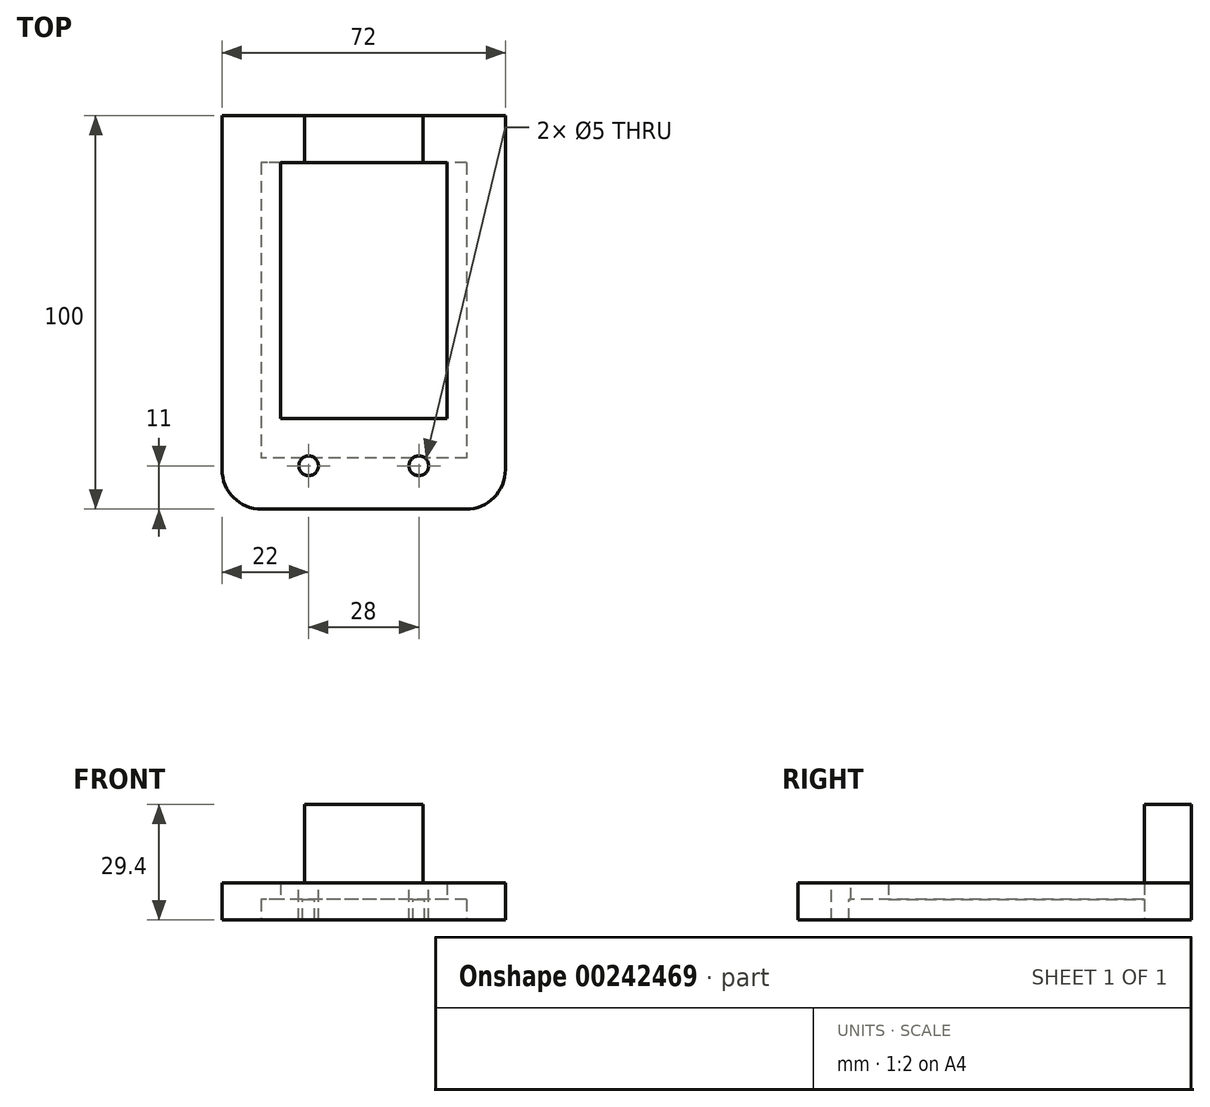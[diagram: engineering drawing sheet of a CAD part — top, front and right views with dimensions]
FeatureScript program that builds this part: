
annotation { "Feature Type Name" : "Feature", "Feature Type Description" : "" }
export const myFeature = defineFeature(function(context is Context, id is Id, definition is map)
    precondition{}
    {
        {
            var Q0;
            Q0=qCreatedBy(makeId("Top.planeOp"),FACE);
            var sketch = newSketch(context, id + "F0", { "sketchPlane" : qUnion([Q0])});
            skLineSegment(sketch, "E0.bottom", {"start": v(36, 50) * mm, "end": v(-36, 50) * mm});
            skLineSegment(sketch, "E0.top", {"start": v(36, -50) * mm, "end": v(-36, -50) * mm});
            skLineSegment(sketch, "E0.left", {"start": v(36, 50) * mm, "end": v(36, -50) * mm});
            skLineSegment(sketch, "E0.right", {"start": v(-36, 50) * mm, "end": v(-36, -50) * mm});
            skPoint(sketch, "E0.middle", {"position": v(0, 0) * mm});
            skSolve(sketch);
        }
        {
            var Q0;
            Q0=makeQuery(id+"F0.imprint","IMPRINT",FACE,{"disambiguationData":[TD([[makeQuery(id+"F0.imprint","IMPRINT",EDGE,{"derivedFrom":sQuery(id+"F0.wireOp",EDGE,"E0.bottom")}),1.0]])]});
            extrude(context, id + "F1", {"entities" : qUnion([Q0]), "depth" : 9.4 * mm});
        }
        {
            var Q0;
            Q0=makeQuery(id+"F1.opExtrude","CAP_FACE",FACE,{"disambiguationData":[OSD([sQuery(id+"F0.wireOp",EDGE,"E0.bottom"),sQuery(id+"F0.wireOp",EDGE,"E0.top"),sQuery(id+"F0.wireOp",EDGE,"E0.left"),sQuery(id+"F0.wireOp",EDGE,"E0.right")])],"isStart":true});
            var sketch = newSketch(context, id + "F2", { "sketchPlane" : qUnion([Q0])});
            skLineSegment(sketch, "E1.bottom", {"start": v(26.15, -38) * mm, "end": v(-26.15, -38) * mm});
            skLineSegment(sketch, "E1.top", {"start": v(26.15, 37) * mm, "end": v(-26.15, 37) * mm});
            skLineSegment(sketch, "E1.left", {"start": v(26.15, -38) * mm, "end": v(26.15, 37) * mm});
            skLineSegment(sketch, "E1.right", {"start": v(-26.15, -38) * mm, "end": v(-26.15, 37) * mm});
            skPoint(sketch, "E1.middle", {"position": v(0, -0.5) * mm});
            skLineSegment(sketch, "E2.bottom", {"start": v(21.1, 27) * mm, "end": v(-21.1, 27) * mm});
            skLineSegment(sketch, "E2.top", {"start": v(21.1, -38) * mm, "end": v(-21.1, -38) * mm});
            skLineSegment(sketch, "E2.left", {"start": v(21.1, 27) * mm, "end": v(21.1, -38) * mm});
            skLineSegment(sketch, "E2.right", {"start": v(-21.1, 27) * mm, "end": v(-21.1, -38) * mm});
            skPoint(sketch, "E2.middle", {"position": v(0, -5.5) * mm});
            skPoint(sketch, "E3", {"position": v(0, -38) * mm});
            skSolve(sketch);
        }
        {
            var Q0;
            Q0=makeQuery(id+"F2.imprint","IMPRINT",FACE,{"disambiguationData":[TD([[makeQuery(id+"F2.imprint","IMPRINT",EDGE,{"derivedFrom":sQuery(id+"F2.wireOp",EDGE,"E1.bottom")}),-1.0]])]});
            var Q1;
            Q1=makeQuery(id+"F2.imprint","IMPRINT",FACE,{"disambiguationData":[TD([[makeQuery(id+"F2.imprint","IMPRINT",EDGE,{"derivedFrom":sQuery(id+"F2.wireOp",EDGE,"E2.bottom")}),1.0]])]});
            var Q2;
            {var subQ5=sQuery(id+"F2.wireOp",EDGE,"E2.top");Q2=makeQuery(id+"F2.imprint","IMPRINT",FACE,{"disambiguationData":[TD([[makeQuery(id+"F2.imprint","IMPRINT",EDGE,{"derivedFrom":subQ5}),-1.0]])]});}
            extrude(context, id + "F3", {"entities" : qUnion([Q0, Q1, Q2]), "operationType" : NewBodyOperationType.REMOVE, "oppositeDirection" : true, "depth" : 5.2 * mm});
        }
        {
            var Q0;
            Q0=makeQuery(id+"F2.imprint","IMPRINT",FACE,{"disambiguationData":[TD([[makeQuery(id+"F2.imprint","IMPRINT",EDGE,{"derivedFrom":sQuery(id+"F2.wireOp",EDGE,"E2.bottom")}),1.0]])]});
            var Q1;
            {var subQ5=sQuery(id+"F2.wireOp",EDGE,"E2.top");Q1=makeQuery(id+"F2.imprint","IMPRINT",FACE,{"disambiguationData":[TD([[makeQuery(id+"F2.imprint","IMPRINT",EDGE,{"derivedFrom":subQ5}),-1.0]])]});}
            var Q2;
            Q2=makeQuery(id+"F1.opExtrude","CAP_FACE",FACE,{"disambiguationData":[OSD([sQuery(id+"F0.wireOp",EDGE,"E0.bottom"),sQuery(id+"F0.wireOp",EDGE,"E0.top"),sQuery(id+"F0.wireOp",EDGE,"E0.left"),sQuery(id+"F0.wireOp",EDGE,"E0.right")])],"isStart":false});
            extrude(context, id + "F4", {"entities" : qUnion([Q0, Q1]), "operationType" : NewBodyOperationType.REMOVE, "endBound" : BoundingType.UP_TO_SURFACE, "oppositeDirection" : true, "endBoundEntityFace" : qUnion([Q2]), "depth" : 25 * mm});
        }
        {
            var Q0;
            Q0=makeQuery(id+"F1.opExtrude","CAP_FACE",FACE,{"disambiguationData":[OSD([sQuery(id+"F0.wireOp",EDGE,"E0.bottom"),sQuery(id+"F0.wireOp",EDGE,"E0.top"),sQuery(id+"F0.wireOp",EDGE,"E0.left"),sQuery(id+"F0.wireOp",EDGE,"E0.right")])],"isStart":false});
            var sketch = newSketch(context, id + "F5", { "sketchPlane" : qUnion([Q0])});
            skLineSegment(sketch, "E4.bottom", {"start": v(-15, 50) * mm, "end": v(15, 50) * mm});
            skLineSegment(sketch, "E4.top", {"start": v(-15, 38) * mm, "end": v(15, 38) * mm});
            skLineSegment(sketch, "E4.left", {"start": v(-15, 50) * mm, "end": v(-15, 38) * mm});
            skLineSegment(sketch, "E4.right", {"start": v(15, 50) * mm, "end": v(15, 38) * mm});
            skPoint(sketch, "E5", {"position": v(0, 50) * mm});
            skSolve(sketch);
        }
        {
            var Q0;
            Q0=makeQuery(id+"F5.imprint","IMPRINT",FACE,{"disambiguationData":[TD([[makeQuery(id+"F5.imprint","IMPRINT",EDGE,{"derivedFrom":sQuery(id+"F5.wireOp",EDGE,"xHcaIH9m-dqr2-VmLf-LCX5-amg7zSHhJgyx.bottom")}),-1.0]])]});
            var Q1;
            Q1=makeQuery(id+"F5.imprint","IMPRINT",FACE,{"disambiguationData":[TD([[makeQuery(id+"F5.imprint","IMPRINT",EDGE,{"derivedFrom":sQuery(id+"F5.wireOp",EDGE,"E4.bottom")}),1.0]])]});
            extrude(context, id + "F6", {"entities" : qUnion([Q0, Q1]), "operationType" : NewBodyOperationType.ADD, "depth" : 20 * mm});
        }
        {
            var Q0;
            Q0=makeQuery(id+"F1.opExtrude","CAP_FACE",FACE,{"disambiguationData":[OSD([sQuery(id+"F0.wireOp",EDGE,"E0.bottom"),sQuery(id+"F0.wireOp",EDGE,"E0.top"),sQuery(id+"F0.wireOp",EDGE,"E0.left"),sQuery(id+"F0.wireOp",EDGE,"E0.right")])],"isStart":false});
            var sketch = newSketch(context, id + "F7", { "sketchPlane" : qUnion([Q0])});
            skLineSegment(sketch, "E6", {"start": v(-36, -39) * mm, "end": v(36, -39) * mm, "construction": true});
            skCircle(sketch, "E7", {"center": v(-14, -39) * mm, "radius": 2.5 * mm});
            skCircle(sketch, "E8", {"center": v(14, -39) * mm, "radius": 2.5 * mm});
            skSolve(sketch);
        }
        {
            var Q0;
            Q0=makeQuery(id+"F7.imprint","IMPRINT",FACE,{"disambiguationData":[TD([[makeQuery(id+"F7.imprint","IMPRINT",EDGE,{"derivedFrom":sQuery(id+"F7.wireOp",EDGE,"E7")}),1.0]])]});
            var Q1;
            Q1=makeQuery(id+"F7.imprint","IMPRINT",FACE,{"disambiguationData":[TD([[makeQuery(id+"F7.imprint","IMPRINT",EDGE,{"derivedFrom":sQuery(id+"F7.wireOp",EDGE,"E8")}),1.0]])]});
            var Q2;
            Q2=makeQuery(id+"F1.opExtrude","CAP_FACE",FACE,{"disambiguationData":[OSD([sQuery(id+"F0.wireOp",EDGE,"E0.bottom"),sQuery(id+"F0.wireOp",EDGE,"E0.top"),sQuery(id+"F0.wireOp",EDGE,"E0.left"),sQuery(id+"F0.wireOp",EDGE,"E0.right")])],"isStart":true});
            extrude(context, id + "F8", {"entities" : qUnion([Q0, Q1]), "operationType" : NewBodyOperationType.REMOVE, "endBound" : BoundingType.UP_TO_SURFACE, "oppositeDirection" : true, "endBoundEntityFace" : qUnion([Q2]), "depth" : 25 * mm});
        }
        {
            var Q0;
            Q0=makeQuery(id+"F1.opExtrude","SWEPT_EDGE",EDGE,{"disambiguationData":[OSD([sQuery(id+"F0.wireOp",EDGE,"E0.top"),sQuery(id+"F0.wireOp",EDGE,"E0.left")])]});
            var Q1;
            Q1=makeQuery(id+"F1.opExtrude","SWEPT_EDGE",EDGE,{"disambiguationData":[OSD([sQuery(id+"F0.wireOp",EDGE,"E0.top"),sQuery(id+"F0.wireOp",EDGE,"E0.right")])]});
            fillet(context, id + "F9", {"entities" : qUnion([Q0, Q1]), "radius" : 10 * mm, "tangentPropagation" : true, "allowEdgeOverflow" : false});
        }
    });
